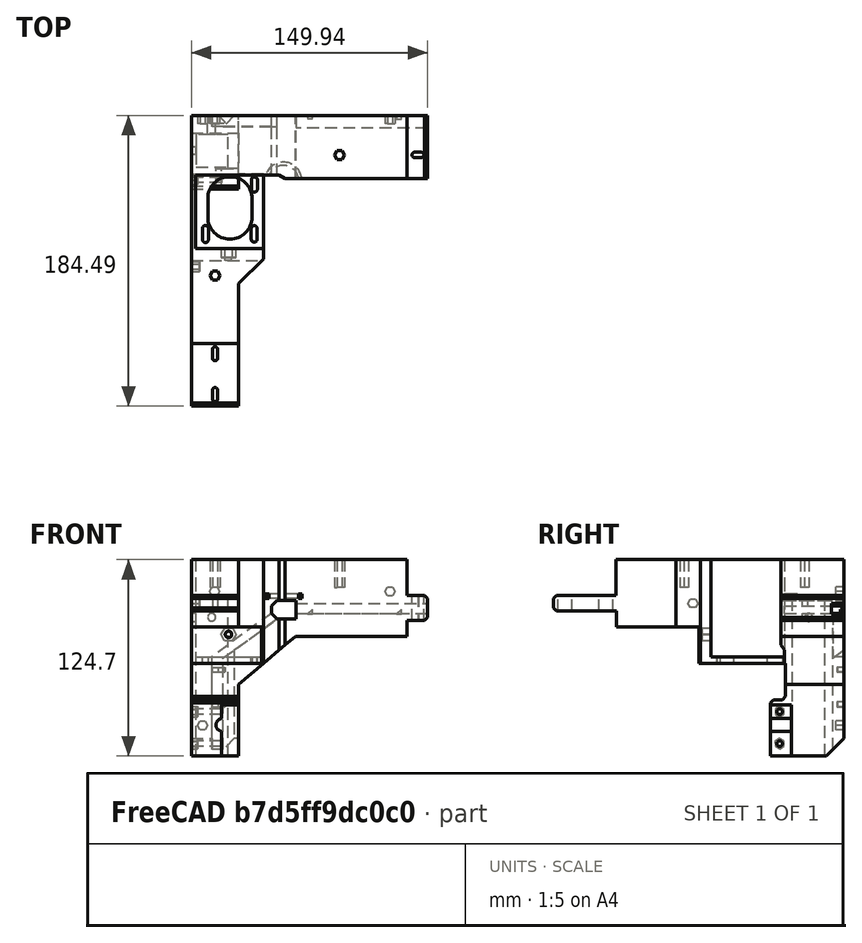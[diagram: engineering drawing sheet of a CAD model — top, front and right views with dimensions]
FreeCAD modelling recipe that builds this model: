
FCSTD DOCUMENT  (FreeCAD 0.21R33771 (Git))
Label: TOP_left_rear_frame_extrusion
License: All rights reserved
LicenseURL: http://en.wikipedia.org/wiki/All_rights_reserved
objects: Sketcher::SketchObject×2, PartDesign::Pocket×2, Part::Feature×1, PartDesign::FeatureBase×1, PartDesign::Body×1
note: 9 computed .brp shape members not serialized (recipe doc carries the construction recipe); baked Part::Feature solids carry a one-line shape summary decoded from their .brp

FEATURE [Part::Feature] Part__Feature  label="TOP_Left_Rear_Frame_extrusion"
  shape: bbox 149.9 x 184.5 x 124.7 mm, 186 faces (baked)
FEATURE [PartDesign::FeatureBase] BaseFeature
  BaseFeature = -> Part__Feature
FEATURE [Sketcher::SketchObject] Sketch
  FullyConstrained = false
  MapMode = 5
  Placement = pos=(0,0,45.9983) rot=(0,0,1;0rad)
  Support = -> [BaseFeature]
  sketch-geometry (8):
    g0: ArcOfCircle CenterX=-59.9819 CenterY=-56.307 CenterZ=0 NormalX=0 NormalY=0 NormalZ=1 AngleXU=0 Radius=1.68543 StartAngle=0 EndAngle=3.14159
    g1: ArcOfCircle CenterX=-59.9819 CenterY=-61.8026 CenterZ=0 NormalX=0 NormalY=0 NormalZ=1 AngleXU=0 Radius=1.68543 StartAngle=3.14159 EndAngle=6.28319
    g2: LineSegment StartX=-61.6673 StartY=-56.307 StartZ=0 EndX=-61.6673 EndY=-61.8026 EndZ=0
    g3: LineSegment StartX=-58.2964 StartY=-61.8026 StartZ=0 EndX=-58.2964 EndY=-56.307 EndZ=0
    g4: ArcOfCircle CenterX=-59.9726 CenterY=-82.3001 CenterZ=0 NormalX=0 NormalY=0 NormalZ=1 AngleXU=0 Radius=1.70546 StartAngle=1e-16 EndAngle=3.14159
    g5: ArcOfCircle CenterX=-59.9726 CenterY=-87.7956 CenterZ=0 NormalX=0 NormalY=0 NormalZ=1 AngleXU=0 Radius=1.70546 StartAngle=3.14159 EndAngle=6.28319
    g6: LineSegment StartX=-61.6781 StartY=-82.3001 StartZ=0 EndX=-61.6781 EndY=-87.7956 EndZ=0
    g7: LineSegment StartX=-58.2672 StartY=-87.7956 StartZ=0 EndX=-58.2672 EndY=-82.3001 EndZ=0
  constraints (12):
    c: Tangent(g0,g2) = -1.5708
    c: Tangent(g2,g1) = -1.5708
    c: Tangent(g1,g3) = -1.5708
    c: Tangent(g3,g0) = -1.5708
    c: Equal(g0,g1)
    c: Vertical(g2)
    c: Tangent(g4,g6) = -1.5708
    c: Tangent(g6,g5) = -1.5708
    c: Tangent(g5,g7) = -1.5708
    c: Tangent(g7,g4) = -1.5708
    c: Equal(g4,g5)
    c: Vertical(g6)
FEATURE [PartDesign::Pocket] Pocket
  BaseFeature = -> BaseFeature
  Direction = (0,0,-1)
  Length = 17
  Length2 = 5
  Profile = -> Sketch
  ReferenceAxis = -> Sketch [N_Axis]
  Refine = true
  Type = 0
FEATURE [Sketcher::SketchObject] Sketch001
  FullyConstrained = false
  MapMode = 5
  Placement = pos=(0,0,45.9949) rot=(0,0,1;0rad)
  Support = -> [Pocket]
  sketch-geometry (4):
    g0: ArcOfCircle CenterX=66.8279 CenterY=67.1956 CenterZ=0 NormalX=0 NormalY=0 NormalZ=1 AngleXU=0 Radius=1.70458 StartAngle=1.5708 EndAngle=4.71239
    g1: ArcOfCircle CenterX=70.9331 CenterY=67.1956 CenterZ=0 NormalX=0 NormalY=0 NormalZ=1 AngleXU=0 Radius=1.70458 StartAngle=4.71239 EndAngle=7.85398
    g2: LineSegment StartX=66.8279 StartY=65.491 StartZ=0 EndX=70.9331 EndY=65.491 EndZ=0
    g3: LineSegment StartX=70.9331 StartY=68.9002 StartZ=0 EndX=66.8279 EndY=68.9002 EndZ=0
  constraints (6):
    c: Tangent(g0,g2) = -1.5708
    c: Tangent(g2,g1) = -1.5708
    c: Tangent(g1,g3) = -1.5708
    c: Tangent(g3,g0) = -1.5708
    c: Equal(g0,g1)
    c: Horizontal(g2)
FEATURE [PartDesign::Pocket] Pocket001
  BaseFeature = -> Pocket
  Direction = (0,0,-1)
  Length = 5
  Length2 = 5
  Profile = -> Sketch001
  ReferenceAxis = -> Sketch001 [N_Axis]
  Refine = true
  Type = 1
FEATURE [PartDesign::Body] Body
  BaseFeature = -> Part__Feature
  Group = -> [BaseFeature,Sketch,Pocket,Sketch001,Pocket001]
  Origin = -> Origin
  Tip = -> Pocket001
